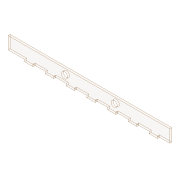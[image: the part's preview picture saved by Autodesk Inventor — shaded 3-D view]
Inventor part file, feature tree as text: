
AUTODESK INVENTOR PART (.ipt)
format: ipt  version: 2020 (Build 240168000, 168)  size: 148,480 bytes
history: native  units: mm
features: extrude x3, sketch x3
ambient origin geometry x8: Origin, YZ Plane, XZ Plane, XY Plane, X Axis, Y Axis, Z Axis, Center Point
bodies: Solid1 (feature_tree)
feature tree (6):
  extrude  "Base"  Depth=30.0mm
  extrude  "Extrusion3"  Depth=5.0mm
  extrude  "Extrusion4"  Depth=10.0mm TaperAngle=0.0deg
  sketch  "Sketch1"  dims[d0=390.0mm d1=30.0mm]
  sketch  "Sketch3"  dims[d2=5.0mm d3=0.0mm d16=15.0mm]
  sketch  "Sketch4"  dims[d17=15.0mm d18=10.0mm d19=0.0mm d20=134.3mm d22=120.0mm d23=20.0mm d24=5.0mm d25=30.0mm d26=70.0mm d28=50.0mm d29=10.0mm d31=10.0mm d33=5.0mm d34=0.0mm]
